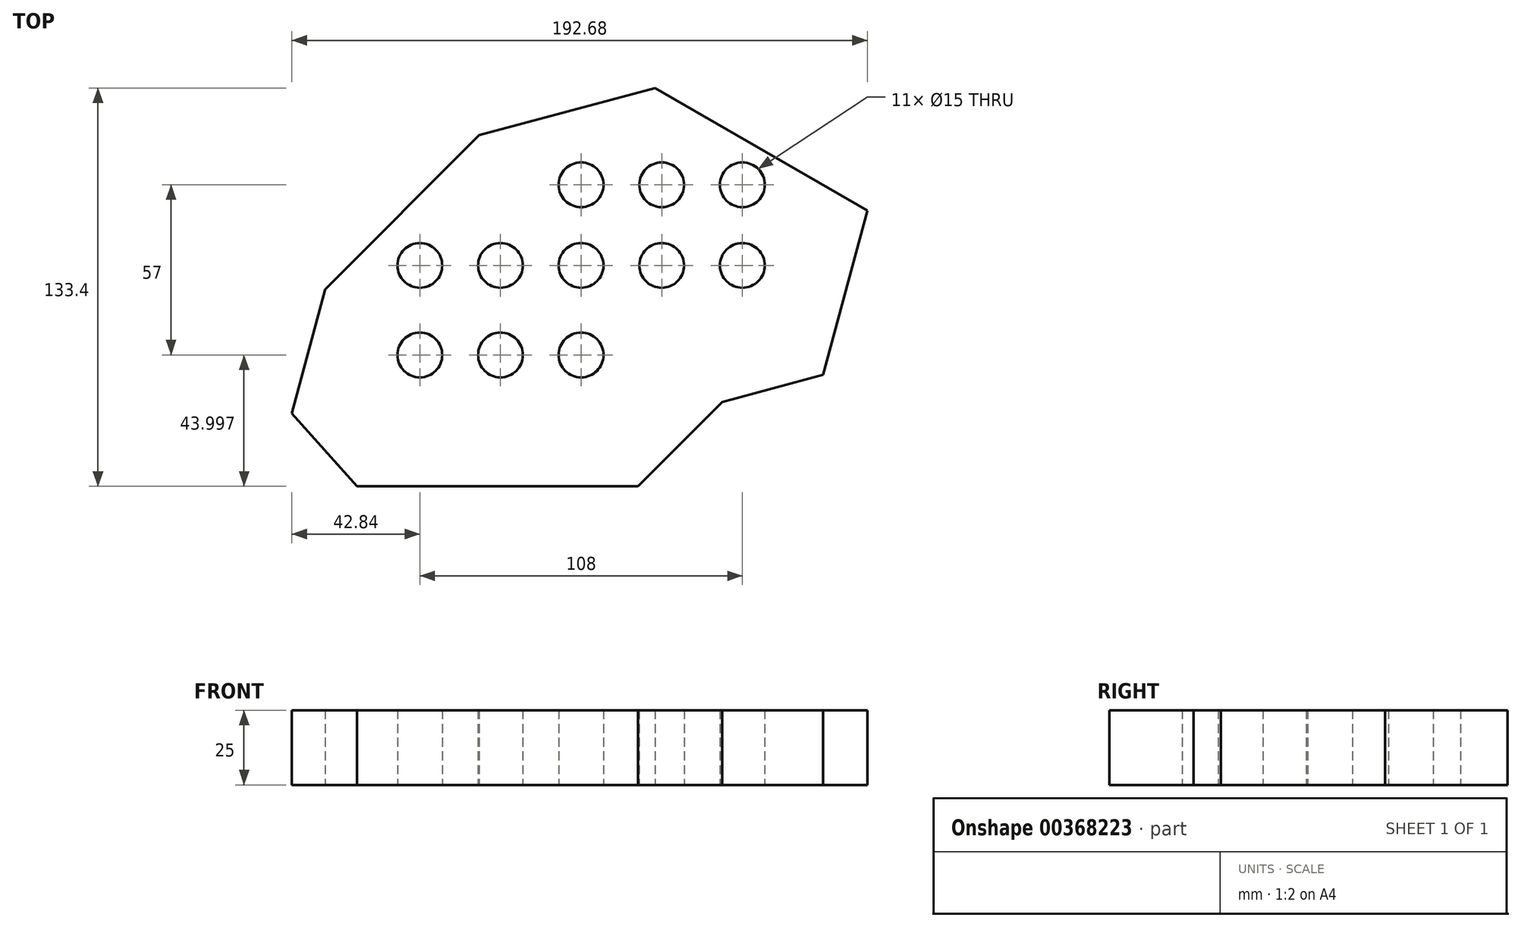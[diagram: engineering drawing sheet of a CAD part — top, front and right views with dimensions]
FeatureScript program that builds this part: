
annotation { "Feature Type Name" : "Feature", "Feature Type Description" : "" }
export const myFeature = defineFeature(function(context is Context, id is Id, definition is map)
    precondition{}
    {
        {
            var Q0;
            Q0=qCreatedBy(makeId("Top.planeOp"),FACE);
            var sketch = newSketch(context, id + "F0", { "sketchPlane" : qUnion([Q0])});
            skLineSegment(sketch, "E0", {"start": v(-75, -61.02) * mm, "end": v(19, -61.02) * mm});
            skLineSegment(sketch, "E1", {"start": v(19, -61.02) * mm, "end": v(47.28, -32.74) * mm});
            skLineSegment(sketch, "E2", {"start": v(47.28, -32.74) * mm, "end": v(81.1, -23.68) * mm});
            skLineSegment(sketch, "E3", {"start": v(81.1, -23.68) * mm, "end": v(95.84, 31.38) * mm});
            skLineSegment(sketch, "E4", {"start": v(95.84, 31.38) * mm, "end": v(24.83, 72.38) * mm});
            skLineSegment(sketch, "E5", {"start": v(24.83, 72.38) * mm, "end": v(-34.1, 56.59) * mm});
            skLineSegment(sketch, "E6", {"start": v(-34.1, 56.59) * mm, "end": v(-85.7, 4.97) * mm});
            skLineSegment(sketch, "E7", {"start": v(-85.7, 4.97) * mm, "end": v(-96.84, -36.56) * mm});
            skLineSegment(sketch, "E8", {"start": v(-96.84, -36.56) * mm, "end": v(-75, -61.02) * mm});
            skLineSegment(sketch, "E9", {"start": v(-54, -61.02) * mm, "end": v(-54, -17.02) * mm, "construction": true});
            skLineSegment(sketch, "E10", {"start": v(-54, -17.02) * mm, "end": v(-54, 12.98) * mm, "construction": true});
            skPoint(sketch, "E11", {"position": v(-27, -17.02) * mm});
            skCircle(sketch, "E12", {"center": v(-54, -17.02) * mm, "radius": 7.5 * mm});
            skLineSegment(sketch, "E13.direction1", {"start": v(-54, -17.02) * mm, "end": v(-29, -17.02) * mm, "construction": true});
            skCircle(sketch, "E14", {"center": v(-54, 12.98) * mm, "radius": 7.5 * mm});
            skCircle(sketch, "E15", {"center": v(-27, -17.02) * mm, "radius": 7.5 * mm});
            skLineSegment(sketch, "E16", {"start": v(-27, -17.02) * mm, "end": v(0, -17.02) * mm, "construction": true});
            skLineSegment(sketch, "E17", {"start": v(-54, 12.98) * mm, "end": v(-27, 12.98) * mm, "construction": true});
            skLineSegment(sketch, "E18", {"start": v(-27, 12.98) * mm, "end": v(0, 12.98) * mm, "construction": true});
            skLineSegment(sketch, "E19", {"start": v(0, 12.98) * mm, "end": v(27, 12.98) * mm, "construction": true});
            skLineSegment(sketch, "E20", {"start": v(27, 12.98) * mm, "end": v(54, 12.98) * mm, "construction": true});
            skCircle(sketch, "E21", {"center": v(-27, 12.98) * mm, "radius": 7.5 * mm});
            skCircle(sketch, "E22", {"center": v(0, 12.98) * mm, "radius": 7.5 * mm});
            skCircle(sketch, "E23", {"center": v(27, 12.98) * mm, "radius": 7.5 * mm});
            skCircle(sketch, "E24", {"center": v(54, 12.98) * mm, "radius": 7.5 * mm});
            skCircle(sketch, "E25", {"center": v(0, -17.02) * mm, "radius": 7.5 * mm});
            skLineSegment(sketch, "E26", {"start": v(0, 12.98) * mm, "end": v(0, 39.98) * mm, "construction": true});
            skLineSegment(sketch, "E27", {"start": v(27, 12.98) * mm, "end": v(27, 39.98) * mm, "construction": true});
            skLineSegment(sketch, "E28", {"start": v(54, 12.98) * mm, "end": v(54, 39.98) * mm, "construction": true});
            skCircle(sketch, "E29", {"center": v(0, 39.98) * mm, "radius": 7.5 * mm});
            skCircle(sketch, "E30", {"center": v(27, 39.98) * mm, "radius": 7.5 * mm});
            skCircle(sketch, "E31", {"center": v(54, 39.98) * mm, "radius": 7.5 * mm});
            skSolve(sketch);
        }
        {
            var Q0;
            Q0=makeQuery(id+"F0.imprint","IMPRINT",FACE,{"disambiguationData":[TD([[makeQuery(id+"F0.imprint","IMPRINT",EDGE,{"derivedFrom":sQuery(id+"F0.wireOp",EDGE,"E0")}),1.0]])]});
            extrude(context, id + "F1", {"entities" : qUnion([Q0]), "depth" : 25 * mm});
        }
    });
